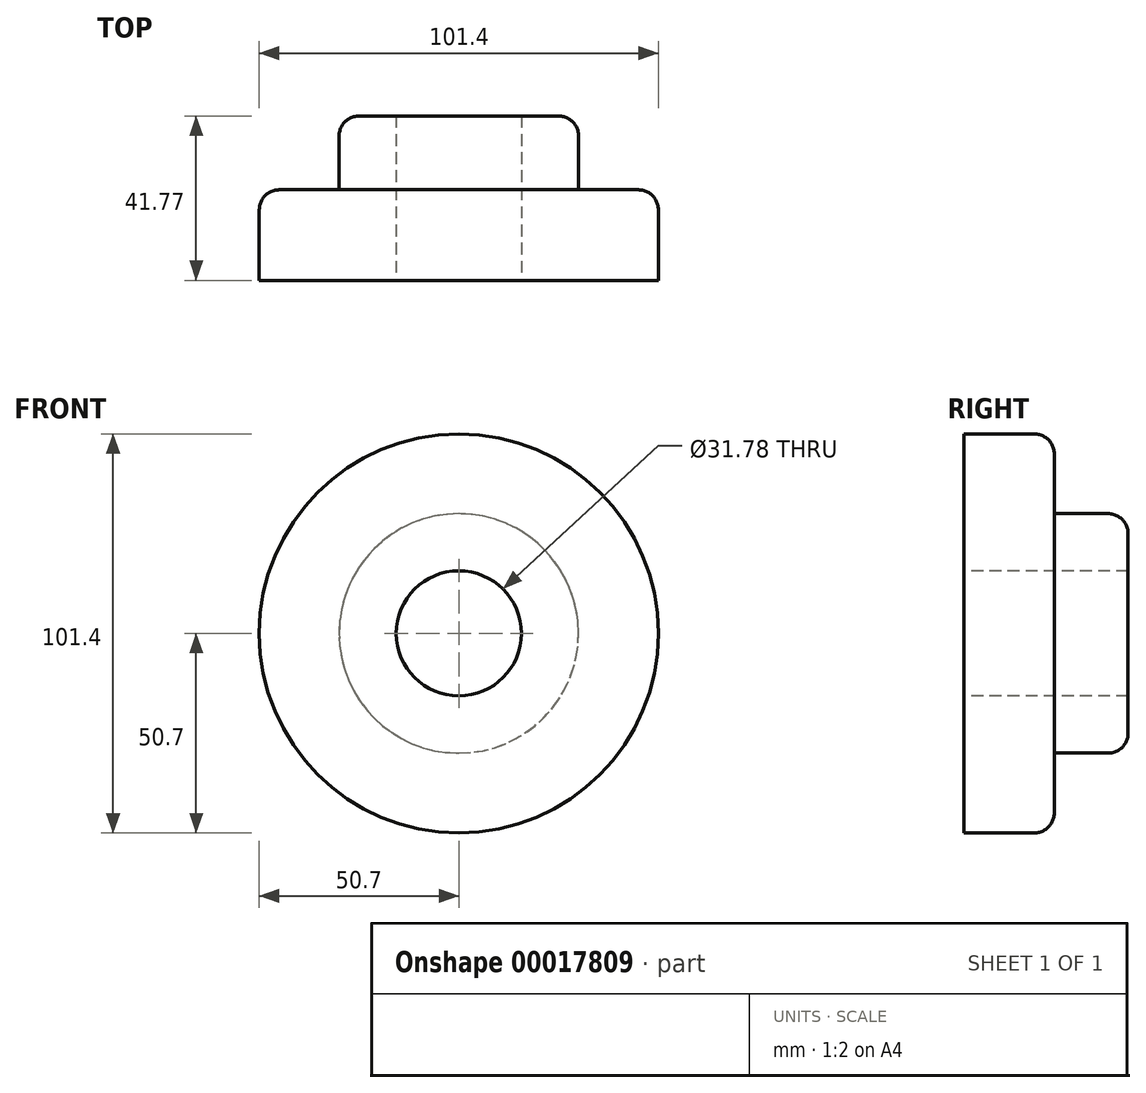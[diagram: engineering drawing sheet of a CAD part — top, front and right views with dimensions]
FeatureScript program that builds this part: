
annotation { "Feature Type Name" : "Feature", "Feature Type Description" : "" }
export const myFeature = defineFeature(function(context is Context, id is Id, definition is map)
    precondition{}
    {
        {
            var Q0;
            Q0=qCreatedBy(makeId("Right.planeOp"),FACE);
            var sketch = newSketch(context, id + "F0", { "sketchPlane" : qUnion([Q0])});
            skLineSegment(sketch, "E0", {"start": v(-48.43, 0) * mm, "end": v(52.97, 0) * mm});
            skLineSegment(sketch, "E1.bottom", {"start": v(-47.52, 50.7) * mm, "end": v(-24.52, 50.7) * mm});
            skLineSegment(sketch, "E1.top", {"start": v(-47.52, 15.89) * mm, "end": v(-24.52, 15.89) * mm});
            skLineSegment(sketch, "E1.left", {"start": v(-47.52, 50.7) * mm, "end": v(-47.52, 15.89) * mm});
            skLineSegment(sketch, "E1.right", {"start": v(-24.52, 50.7) * mm, "end": v(-24.52, 15.89) * mm});
            skLineSegment(sketch, "E2.bottom", {"start": v(-5.75, 30.42) * mm, "end": v(-24.52, 30.42) * mm});
            skLineSegment(sketch, "E2.top", {"start": v(-5.75, 15.89) * mm, "end": v(-24.52, 15.89) * mm});
            skLineSegment(sketch, "E2.left", {"start": v(-5.75, 30.42) * mm, "end": v(-5.75, 15.89) * mm});
            skLineSegment(sketch, "E2.right", {"start": v(-24.52, 30.42) * mm, "end": v(-24.52, 15.89) * mm});
            skSolve(sketch);
        }
        {
            var Q0;
            Q0=makeQuery(id+"F0.imprint","IMPRINT",FACE,{"disambiguationData":[TD([[makeQuery(id+"F0.imprint","IMPRINT",EDGE,{"derivedFrom":sQuery(id+"F0.wireOp",EDGE,"E1.bottom")}),-1.0]])]});
            var Q1;
            Q1=makeQuery(id+"F0.imprint","IMPRINT",FACE,{"disambiguationData":[TD([[makeQuery(id+"F0.imprint","IMPRINT",EDGE,{"derivedFrom":sQuery(id+"F0.wireOp",EDGE,"E2.bottom")}),1.0]])]});
            var Q2;
            Q2=sQuery(id+"F0.wireOp",EDGE,"E0");
            revolve(context, id + "F1", {"entities" : qUnion([Q0, Q1]), "axis" : qUnion([Q2]), "revolveType" : RevolveType.FULL});
        }
        {
            var Q0;
            Q0=makeQuery(id+"F1.opRevolve","SWEPT_EDGE",EDGE,{"disambiguationData":[OSD([sQuery(id+"F0.wireOp",EDGE,"E2.bottom"),sQuery(id+"F0.wireOp",EDGE,"E2.left")])]});
            var Q1;
            Q1=makeQuery(id+"F1.opRevolve","SWEPT_EDGE",EDGE,{"disambiguationData":[OSD([sQuery(id+"F0.wireOp",EDGE,"E1.bottom"),sQuery(id+"F0.wireOp",EDGE,"E1.right")])]});
            fillet(context, id + "F2", {"entities" : qUnion([Q0, Q1]), "radius" : 5.08 * mm, "tangentPropagation" : true, "allowEdgeOverflow" : false});
        }
    });
